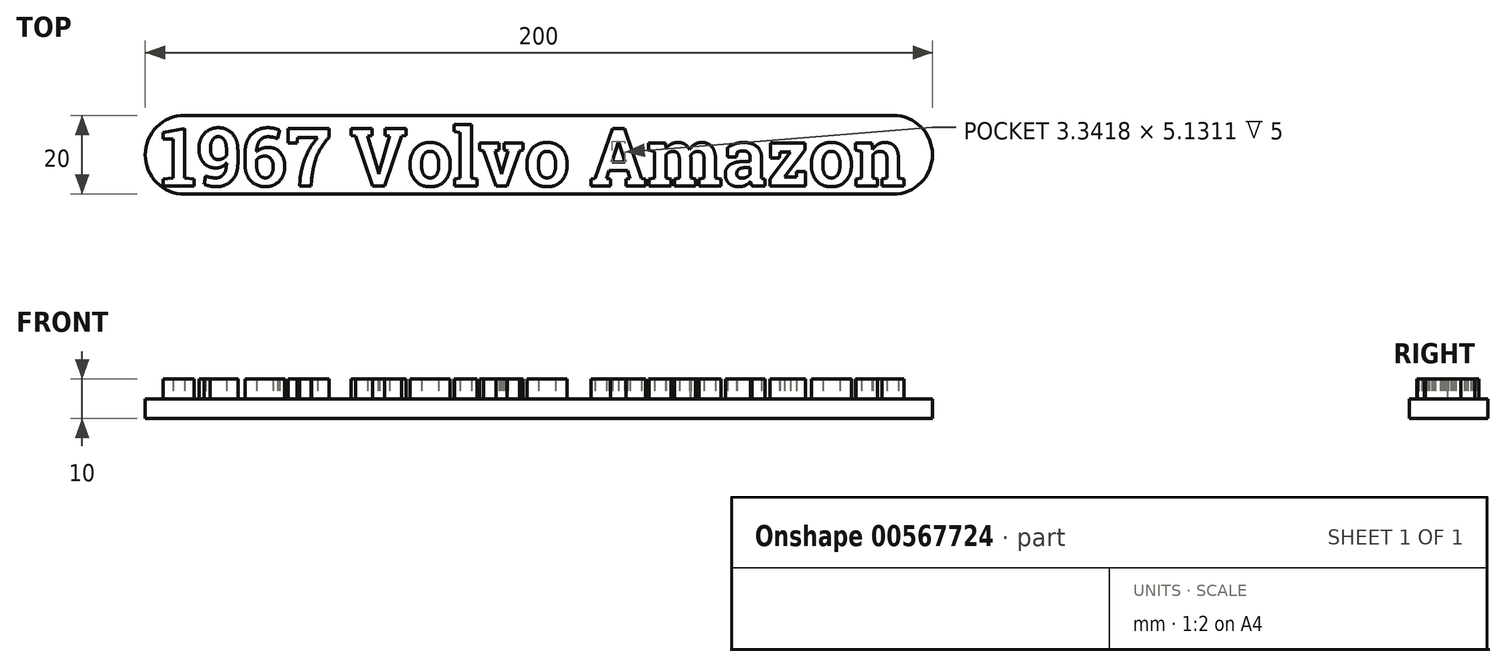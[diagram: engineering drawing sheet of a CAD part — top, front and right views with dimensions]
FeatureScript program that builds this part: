
annotation { "Feature Type Name" : "Feature", "Feature Type Description" : "" }
export const myFeature = defineFeature(function(context is Context, id is Id, definition is map)
    precondition{}
    {
        {
            var Q0;
            Q0=qCreatedBy(makeId("Top.planeOp"),FACE);
            var sketch = newSketch(context, id + "F0", { "sketchPlane" : qUnion([Q0])});
            skLineSegment(sketch, "E0.bottom", {"start": v(-100, 10) * mm, "end": v(100, 10) * mm});
            skLineSegment(sketch, "E0.top", {"start": v(-100, -10) * mm, "end": v(100, -10) * mm});
            skLineSegment(sketch, "E0.left", {"start": v(-100, 10) * mm, "end": v(-100, -10) * mm});
            skLineSegment(sketch, "E0.right", {"start": v(100, 10) * mm, "end": v(100, -10) * mm});
            skPoint(sketch, "E0.middle", {"position": v(0, 0) * mm});
            skSolve(sketch);
        }
        {
            var Q0;
            Q0 = qSketchRegion(id + "F0", true);
            extrude(context, id + "F1", {"entities" : qUnion([Q0]), "depth" : 5 * mm, "offsetDistance" : 25 * mm});
        }
        {
            var Q0;
            Q0=makeQuery(id+"F1.opExtrude","CAP_FACE",FACE,{"disambiguationData":[OSD([sQuery(id+"F0.wireOp",EDGE,"E0.bottom"),sQuery(id+"F0.wireOp",EDGE,"E0.top"),sQuery(id+"F0.wireOp",EDGE,"E0.left"),sQuery(id+"F0.wireOp",EDGE,"E0.right")])],"isStart":false});
            var sketch = newSketch(context, id + "F2", { "sketchPlane" : qUnion([Q0])});
            skText(sketch, "E1", { "text": "1967 Volvo Amazon", "fontName": "RobotoSlab-Bold.ttf"});
            const initialGuessF2  = {"E1": [-0.09604, -0.0079, 1, 0, 0.01475]};
            skSetInitialGuess(sketch, initialGuessF2);
            skSolve(sketch);
        }
        {
            var Q0;
            Q0 = qSketchRegion(id + "F2", true);
            extrude(context, id + "F3", {"entities" : qUnion([Q0]), "operationType" : NewBodyOperationType.ADD, "depth" : 5 * mm, "offsetDistance" : 25 * mm});
        }
        {
            var Q0;
            Q0=makeQuery(id+"F1.opExtrude","SWEPT_EDGE",EDGE,{"disambiguationData":[OSD([sQuery(id+"F0.wireOp",EDGE,"E0.bottom"),sQuery(id+"F0.wireOp",EDGE,"E0.left")])]});
            var Q1;
            Q1=makeQuery(id+"F1.opExtrude","SWEPT_EDGE",EDGE,{"disambiguationData":[OSD([sQuery(id+"F0.wireOp",EDGE,"E0.top"),sQuery(id+"F0.wireOp",EDGE,"E0.left")])]});
            var Q2;
            Q2=makeQuery(id+"F1.opExtrude","SWEPT_EDGE",EDGE,{"disambiguationData":[OSD([sQuery(id+"F0.wireOp",EDGE,"E0.top"),sQuery(id+"F0.wireOp",EDGE,"E0.right")])]});
            var Q3;
            Q3=makeQuery(id+"F1.opExtrude","SWEPT_EDGE",EDGE,{"disambiguationData":[OSD([sQuery(id+"F0.wireOp",EDGE,"E0.bottom"),sQuery(id+"F0.wireOp",EDGE,"E0.right")])]});
            fillet(context, id + "F4", {"entities" : qUnion([Q0, Q1, Q2, Q3]), "radius" : 10 * mm, "tangentPropagation" : true, "allowEdgeOverflow" : false});
        }
    });
